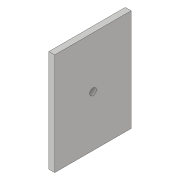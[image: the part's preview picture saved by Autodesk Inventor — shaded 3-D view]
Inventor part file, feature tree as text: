
AUTODESK INVENTOR PART (.ipt)
format: ipt  version: 2017 (Build 210142000, 142)  size: 74,240 bytes
history: native  units: in
note: dims shown in document units (in); Inventor stores cm internally (conversion verified against a paired STEP export)
features: extrude x1, sketch x1
ambient origin geometry x8: Origin, YZ Plane, XZ Plane, XY Plane, X Axis, Y Axis, Z Axis, Center Point
bodies: Solid1 (feature_tree)
feature tree (2):
  extrude  "Extrusion1"  Depth=1.5in
  sketch  "Sketch1"  dims[d0=2.0in d1=1.5in d2=0.13in d3=0.115in d4=0.0in]
